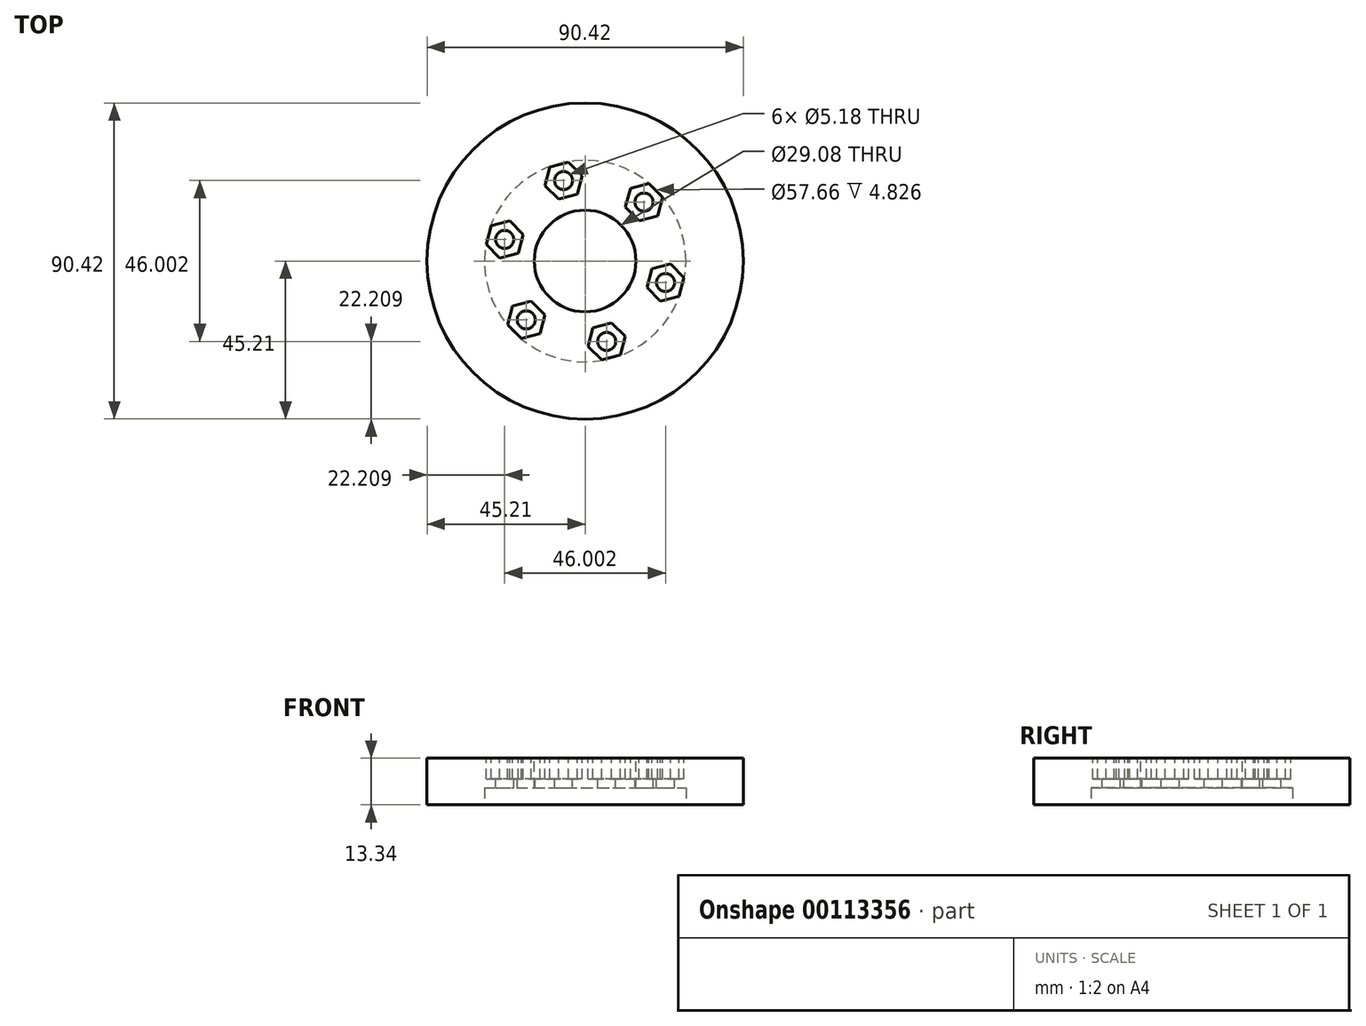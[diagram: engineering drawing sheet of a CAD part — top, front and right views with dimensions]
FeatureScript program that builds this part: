
annotation { "Feature Type Name" : "Feature", "Feature Type Description" : "" }
export const myFeature = defineFeature(function(context is Context, id is Id, definition is map)
    precondition{}
    {
        {
            var Q0;
            Q0=qCreatedBy(makeId("Top.planeOp"),FACE);
            var sketch = newSketch(context, id + "F0", { "sketchPlane" : qUnion([Q0])});
            skCircle(sketch, "E0", {"center": v(0, 0) * mm, "radius": 45.21 * mm});
            skSolve(sketch);
        }
        {
            var Q0;
            Q0=qSketchRegion(id+"F0",true);
            extrude(context, id + "F1", {"entities" : qUnion([Q0]), "depth" : 13.33 * mm, "offsetDistance" : 25.4 * mm});
        }
        {
            var Q0;
            Q0=makeQuery(id+"F1.opExtrude","CAP_FACE",FACE,{"disambiguationData":[OSD([sQuery(id+"F0.wireOp",EDGE,"E0")])],"isStart":false});
            var sketch = newSketch(context, id + "F2", { "sketchPlane" : qUnion([Q0])});
            skLineSegment(sketch, "E1", {"start": v(0, 0) * mm, "end": v(0, 60.06) * mm, "construction": true});
            skLineSegment(sketch, "E2", {"start": v(0, 0) * mm, "end": v(-13.99, 52.2) * mm, "construction": true});
            skCircle(sketch, "E3", {"center": v(0, 0) * mm, "radius": 23.81 * mm, "construction": true});
            skCircle(sketch, "E4", {"center": v(-6.16, 23) * mm, "radius": 2.6 * mm});
            skCircle(sketch, "E5.1.0", {"center": v(-23, 6.16) * mm, "radius": 2.6 * mm});
            skCircle(sketch, "E5.2.0", {"center": v(-16.84, -16.84) * mm, "radius": 2.6 * mm});
            skCircle(sketch, "E6.1.3.0", {"center": v(6.16, -23) * mm, "radius": 2.6 * mm});
            skCircle(sketch, "E6.1.4.0", {"center": v(23, -6.16) * mm, "radius": 2.6 * mm});
            skCircle(sketch, "E6.1.5.0", {"center": v(16.84, 16.84) * mm, "radius": 2.6 * mm});
            skLineSegment(sketch, "E7", {"start": v(0, 0) * mm, "end": v(16.84, 16.84) * mm, "construction": true});
            skSolve(sketch);
        }
        {
            var Q0;
            Q0=makeQuery(id+"F2.imprint","IMPRINT",FACE,{"disambiguationData":[TD([[makeQuery(id+"F2.imprint","IMPRINT",EDGE,{"derivedFrom":sQuery(id+"F2.wireOp",EDGE,"E4")}),1.0]])]});
            var Q1;
            Q1=makeQuery(id+"F2.imprint","IMPRINT",FACE,{"disambiguationData":[TD([[makeQuery(id+"F2.imprint","IMPRINT",EDGE,{"derivedFrom":sQuery(id+"F2.wireOp",EDGE,"E5.1.0")}),1.0]])]});
            var Q2;
            Q2=makeQuery(id+"F2.imprint","IMPRINT",FACE,{"disambiguationData":[TD([[makeQuery(id+"F2.imprint","IMPRINT",EDGE,{"derivedFrom":sQuery(id+"F2.wireOp",EDGE,"E5.2.0")}),1.0]])]});
            var Q3;
            Q3=makeQuery(id+"F2.imprint","IMPRINT",FACE,{"disambiguationData":[TD([[makeQuery(id+"F2.imprint","IMPRINT",EDGE,{"derivedFrom":sQuery(id+"F2.wireOp",EDGE,"E6.1.3.0")}),1.0]])]});
            var Q4;
            Q4=makeQuery(id+"F2.imprint","IMPRINT",FACE,{"disambiguationData":[TD([[makeQuery(id+"F2.imprint","IMPRINT",EDGE,{"derivedFrom":sQuery(id+"F2.wireOp",EDGE,"E6.1.4.0")}),1.0]])]});
            var Q5;
            Q5=makeQuery(id+"F2.imprint","IMPRINT",FACE,{"disambiguationData":[TD([[makeQuery(id+"F2.imprint","IMPRINT",EDGE,{"derivedFrom":sQuery(id+"F2.wireOp",EDGE,"E6.1.5.0")}),1.0]])]});
            extrude(context, id + "F3", {"entities" : qUnion([Q0, Q1, Q2, Q3, Q4, Q5]), "operationType" : NewBodyOperationType.REMOVE, "oppositeDirection" : true, "depth" : 25.4 * mm});
        }
        {
            var Q0;
            Q0=makeQuery(id+"F2.imprint","IMPRINT",FACE,{"disambiguationData":[TD([[makeQuery(id+"F2.imprint","IMPRINT",EDGE,{"derivedFrom":sQuery(id+"F2.wireOp",EDGE,"E4")}),-1.0]])]});
            var sketch = newSketch(context, id + "F4", { "sketchPlane" : qUnion([Q0])});
            skCircle(sketch, "E8", {"center": v(0, 0) * mm, "radius": 14.54 * mm});
            skSolve(sketch);
        }
        {
            var Q0;
            Q0=qSketchRegion(id+"F4",true);
            extrude(context, id + "F5", {"entities" : qUnion([Q0]), "operationType" : NewBodyOperationType.REMOVE, "oppositeDirection" : true, "depth" : 25.4 * mm});
        }
        {
            var Q0;
            Q0=makeQuery(id+"F1.opExtrude","CAP_FACE",FACE,{"disambiguationData":[OSD([sQuery(id+"F0.wireOp",EDGE,"E0")])],"isStart":false});
            var sketch = newSketch(context, id + "F6", { "sketchPlane" : qUnion([Q0])});
            skLineSegment(sketch, "E9", {"start": v(0, 0) * mm, "end": v(0, 45.21) * mm, "construction": true});
            skLineSegment(sketch, "E10", {"start": v(0, 0) * mm, "end": v(-11.7, 43.67) * mm, "construction": true});
            skLineSegment(sketch, "E11", {"start": v(0, 0) * mm, "end": v(31.97, 31.97) * mm, "construction": true});
            skLineSegment(sketch, "E12", {"start": v(0, 0) * mm, "end": v(43.67, -11.7) * mm, "construction": true});
            skLineSegment(sketch, "E13", {"start": v(0, 0) * mm, "end": v(11.7, -43.67) * mm, "construction": true});
            skLineSegment(sketch, "E14", {"start": v(0, 0) * mm, "end": v(-31.97, -31.97) * mm, "construction": true});
            skLineSegment(sketch, "E15", {"start": v(0, 0) * mm, "end": v(-43.67, 11.7) * mm, "construction": true});
            skCircle(sketch, "E16.cCircle", {"center": v(-6.16, 23) * mm, "radius": 4.76 * mm, "construction": true});
            skLineSegment(sketch, "E16.0", {"start": v(-10.05, 26.89) * mm, "end": v(-4.74, 28.31) * mm});
            skLineSegment(sketch, "E16.1", {"start": v(-4.74, 28.31) * mm, "end": v(-0.85, 24.42) * mm});
            skLineSegment(sketch, "E16.2", {"start": v(-0.85, 24.42) * mm, "end": v(-2.27, 19.11) * mm});
            skLineSegment(sketch, "E16.3", {"start": v(-2.27, 19.11) * mm, "end": v(-7.59, 17.69) * mm});
            skLineSegment(sketch, "E16.4", {"start": v(-7.59, 17.69) * mm, "end": v(-11.48, 21.58) * mm});
            skLineSegment(sketch, "E16.5", {"start": v(-11.48, 21.58) * mm, "end": v(-10.05, 26.89) * mm});
            skPoint(sketch, "E16.0.midPoint", {"position": v(-7.4, 27.6) * mm});
            skCircle(sketch, "E17.cCircle", {"center": v(16.84, 16.84) * mm, "radius": 4.76 * mm, "construction": true});
            skLineSegment(sketch, "E17.0", {"start": v(18.26, 22.15) * mm, "end": v(22.15, 18.26) * mm});
            skLineSegment(sketch, "E17.1", {"start": v(22.15, 18.26) * mm, "end": v(20.73, 12.95) * mm});
            skLineSegment(sketch, "E17.2", {"start": v(20.73, 12.95) * mm, "end": v(15.41, 11.53) * mm});
            skLineSegment(sketch, "E17.3", {"start": v(15.41, 11.53) * mm, "end": v(11.53, 15.41) * mm});
            skLineSegment(sketch, "E17.4", {"start": v(11.53, 15.41) * mm, "end": v(12.95, 20.73) * mm});
            skLineSegment(sketch, "E17.5", {"start": v(12.95, 20.73) * mm, "end": v(18.26, 22.15) * mm});
            skPoint(sketch, "E17.0.midPoint", {"position": v(20.2, 20.2) * mm});
            skCircle(sketch, "E18.cCircle", {"center": v(23, -6.16) * mm, "radius": 4.76 * mm, "construction": true});
            skLineSegment(sketch, "E18.0", {"start": v(28.31, -4.74) * mm, "end": v(26.89, -10.05) * mm});
            skLineSegment(sketch, "E18.1", {"start": v(26.89, -10.05) * mm, "end": v(21.58, -11.48) * mm});
            skLineSegment(sketch, "E18.2", {"start": v(21.58, -11.48) * mm, "end": v(17.69, -7.59) * mm});
            skLineSegment(sketch, "E18.3", {"start": v(17.69, -7.59) * mm, "end": v(19.11, -2.27) * mm});
            skLineSegment(sketch, "E18.4", {"start": v(19.11, -2.27) * mm, "end": v(24.42, -0.85) * mm});
            skLineSegment(sketch, "E18.5", {"start": v(24.42, -0.85) * mm, "end": v(28.31, -4.74) * mm});
            skPoint(sketch, "E18.0.midPoint", {"position": v(27.6, -7.4) * mm});
            skCircle(sketch, "E19.cCircle", {"center": v(6.16, -23) * mm, "radius": 4.76 * mm, "construction": true});
            skLineSegment(sketch, "E19.0", {"start": v(10.05, -26.89) * mm, "end": v(4.74, -28.31) * mm});
            skLineSegment(sketch, "E19.1", {"start": v(4.74, -28.31) * mm, "end": v(0.85, -24.42) * mm});
            skLineSegment(sketch, "E19.2", {"start": v(0.85, -24.42) * mm, "end": v(2.27, -19.11) * mm});
            skLineSegment(sketch, "E19.3", {"start": v(2.27, -19.11) * mm, "end": v(7.59, -17.69) * mm});
            skLineSegment(sketch, "E19.4", {"start": v(7.59, -17.69) * mm, "end": v(11.48, -21.58) * mm});
            skLineSegment(sketch, "E19.5", {"start": v(11.48, -21.58) * mm, "end": v(10.05, -26.89) * mm});
            skPoint(sketch, "E19.0.midPoint", {"position": v(7.4, -27.6) * mm});
            skCircle(sketch, "E20.cCircle", {"center": v(-16.84, -16.84) * mm, "radius": 4.76 * mm, "construction": true});
            skLineSegment(sketch, "E20.0", {"start": v(-18.26, -22.15) * mm, "end": v(-22.15, -18.26) * mm});
            skLineSegment(sketch, "E20.1", {"start": v(-22.15, -18.26) * mm, "end": v(-20.73, -12.95) * mm});
            skLineSegment(sketch, "E20.2", {"start": v(-20.73, -12.95) * mm, "end": v(-15.41, -11.53) * mm});
            skLineSegment(sketch, "E20.3", {"start": v(-15.41, -11.53) * mm, "end": v(-11.53, -15.41) * mm});
            skLineSegment(sketch, "E20.4", {"start": v(-11.53, -15.41) * mm, "end": v(-12.95, -20.73) * mm});
            skLineSegment(sketch, "E20.5", {"start": v(-12.95, -20.73) * mm, "end": v(-18.26, -22.15) * mm});
            skPoint(sketch, "E20.0.midPoint", {"position": v(-20.2, -20.2) * mm});
            skCircle(sketch, "E21.cCircle", {"center": v(-23, 6.16) * mm, "radius": 4.76 * mm, "construction": true});
            skLineSegment(sketch, "E21.0", {"start": v(-28.31, 4.74) * mm, "end": v(-26.89, 10.05) * mm});
            skLineSegment(sketch, "E21.1", {"start": v(-26.89, 10.05) * mm, "end": v(-21.58, 11.48) * mm});
            skLineSegment(sketch, "E21.2", {"start": v(-21.58, 11.48) * mm, "end": v(-17.69, 7.59) * mm});
            skLineSegment(sketch, "E21.3", {"start": v(-17.69, 7.59) * mm, "end": v(-19.11, 2.27) * mm});
            skLineSegment(sketch, "E21.4", {"start": v(-19.11, 2.27) * mm, "end": v(-24.42, 0.85) * mm});
            skLineSegment(sketch, "E21.5", {"start": v(-24.42, 0.85) * mm, "end": v(-28.31, 4.74) * mm});
            skPoint(sketch, "E21.0.midPoint", {"position": v(-27.6, 7.4) * mm});
            skSolve(sketch);
        }
        {
            var Q0;
            Q0 = qSketchRegion(id + "F6", true);
            extrude(context, id + "F7", {"entities" : qUnion([Q0]), "operationType" : NewBodyOperationType.REMOVE, "oppositeDirection" : true, "depth" : 5.97 * mm, "offsetDistance" : 25.4 * mm});
        }
        {
            var Q0;
            Q0=makeQuery(id+"F1.opExtrude","CAP_FACE",FACE,{"disambiguationData":[OSD([sQuery(id+"F0.wireOp",EDGE,"E0")])],"isStart":true});
            var sketch = newSketch(context, id + "F8", { "sketchPlane" : qUnion([Q0])});
            skCircle(sketch, "E22", {"center": v(0, 0) * mm, "radius": 28.83 * mm});
            skSolve(sketch);
        }
        {
            var Q0;
            Q0 = qSketchRegion(id + "F8", true);
            extrude(context, id + "F9", {"entities" : qUnion([Q0]), "operationType" : NewBodyOperationType.REMOVE, "oppositeDirection" : true, "depth" : 4.83 * mm, "offsetDistance" : 25.4 * mm});
        }
    });
